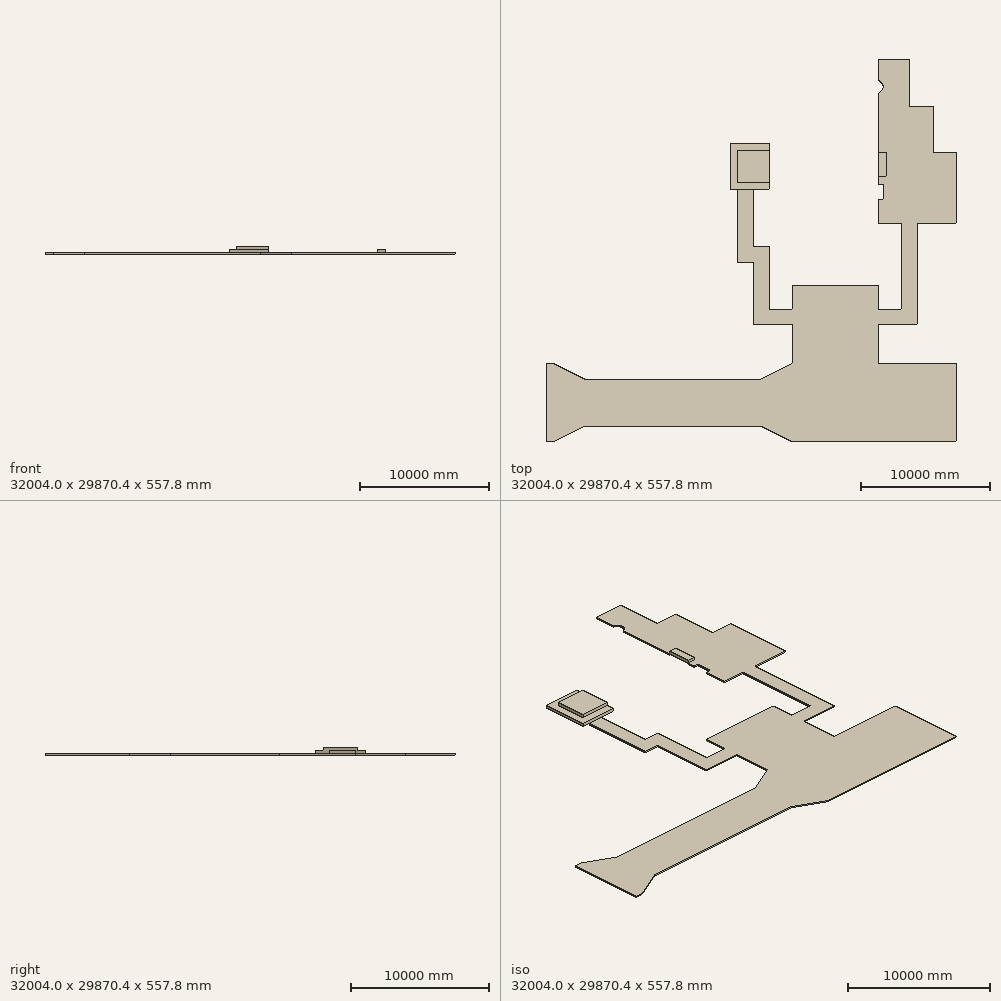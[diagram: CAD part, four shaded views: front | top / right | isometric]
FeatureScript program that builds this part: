
annotation { "Feature Type Name" : "Feature", "Feature Type Description" : "" }
export const myFeature = defineFeature(function(context is Context, id is Id, definition is map)
    precondition{}
    {
        {
            var Q0;
            Q0=qCreatedBy(makeId("Top.planeOp"),FACE);
            var sketch = newSketch(context, id + "F0", { "sketchPlane" : qUnion([Q0])});
            skLineSegment(sketch, "E0", {"start": v(0, 0) * mm, "end": v(-6705.6, 0) * mm});
            skLineSegment(sketch, "E1", {"start": v(-6705.6, 0) * mm, "end": v(-6705.6, 6705.6) * mm, "construction": true});
            skLineSegment(sketch, "E2", {"start": v(-6705.6, 6705.6) * mm, "end": v(-8534.4, 6705.6) * mm, "construction": true});
            skLineSegment(sketch, "E3", {"start": v(-8534.4, 6705.6) * mm, "end": v(-8534.4, 17678.4) * mm, "construction": true});
            skLineSegment(sketch, "E4", {"start": v(-8534.4, 17678.4) * mm, "end": v(0, 17678.4) * mm, "construction": true});
            skLineSegment(sketch, "E5", {"start": v(0, 17678.4) * mm, "end": v(0, 7924.8) * mm});
            skLineSegment(sketch, "E6", {"start": v(-9753.6, 3048) * mm, "end": v(-9753.6, 7467.6) * mm});
            skLineSegment(sketch, "E7", {"start": v(-11582.4, 7467.6) * mm, "end": v(-8534.4, 7467.6) * mm});
            skLineSegment(sketch, "E8", {"start": v(-8534.4, 7467.6) * mm, "end": v(-8534.4, 11125.2) * mm});
            skLineSegment(sketch, "E9", {"start": v(-8534.4, 11125.2) * mm, "end": v(-11582.4, 11125.2) * mm});
            skLineSegment(sketch, "E10", {"start": v(-10972.8, 7467.6) * mm, "end": v(-10972.8, 1828.8) * mm});
            skLineSegment(sketch, "E11", {"start": v(-10972.8, 1828.8) * mm, "end": v(-9753.6, 1828.8) * mm});
            skLineSegment(sketch, "E12", {"start": v(-6705.6, -3048) * mm, "end": v(-6705.6, -6096) * mm});
            skLineSegment(sketch, "E13", {"start": v(-25298.4, -6096) * mm, "end": v(-25908, -6096) * mm});
            skLineSegment(sketch, "E14", {"start": v(-25908, -6096) * mm, "end": v(-25908, -12192) * mm});
            skLineSegment(sketch, "E15", {"start": v(-25908, -12192) * mm, "end": v(-25298.4, -12192) * mm});
            skLineSegment(sketch, "E16", {"start": v(-6705.6, -12192) * mm, "end": v(6096, -12192) * mm});
            skLineSegment(sketch, "E17", {"start": v(6096, -12192) * mm, "end": v(6096, -6096) * mm});
            skLineSegment(sketch, "E18", {"start": v(6096, -6096) * mm, "end": v(0, -6096) * mm});
            skLineSegment(sketch, "E19", {"start": v(0, -6096) * mm, "end": v(0, -3048) * mm});
            skLineSegment(sketch, "E20", {"start": v(0, -3048) * mm, "end": v(3048, -3048) * mm});
            skLineSegment(sketch, "E21", {"start": v(3048, -3048) * mm, "end": v(3048, 4876.8) * mm});
            skLineSegment(sketch, "E22", {"start": v(3048, 4876.8) * mm, "end": v(4267.2, 4876.8) * mm});
            skLineSegment(sketch, "E23", {"start": v(4267.2, 4876.8) * mm, "end": v(4267.2, 4876.8) * mm});
            skLineSegment(sketch, "E24", {"start": v(4267.2, 4876.8) * mm, "end": v(6096, 4876.8) * mm});
            skLineSegment(sketch, "E25", {"start": v(2438.4, 17678.4) * mm, "end": v(0, 17678.4) * mm});
            skLineSegment(sketch, "E26.bottom", {"start": v(-8534.4, 8839.2) * mm, "end": v(-8382, 8839.2) * mm, "construction": true});
            skLineSegment(sketch, "E26.top", {"start": v(-8534.4, 9753.6) * mm, "end": v(-8382, 9753.6) * mm, "construction": true});
            skLineSegment(sketch, "E26.right", {"start": v(-8382, 8839.2) * mm, "end": v(-8382, 9753.6) * mm, "construction": true});
            skLineSegment(sketch, "E27", {"start": v(0, 14020.8) * mm, "end": v(457.2, 13106.4) * mm});
            skLineSegment(sketch, "E28", {"start": v(457.2, 13106.4) * mm, "end": v(457.2, 11277.6) * mm});
            skLineSegment(sketch, "E29", {"start": v(457.2, 11277.6) * mm, "end": v(0, 10363.2) * mm});
            skLineSegment(sketch, "E30.bottom", {"start": v(0, 6324.6) * mm, "end": v(-152.4, 6324.6) * mm, "construction": true});
            skLineSegment(sketch, "E30.top", {"start": v(0, 5410.2) * mm, "end": v(-152.4, 5410.2) * mm, "construction": true});
            skLineSegment(sketch, "E30.left", {"start": v(0, 6324.6) * mm, "end": v(0, 5410.2) * mm, "construction": true});
            skLineSegment(sketch, "E30.right", {"start": v(-152.4, 6324.6) * mm, "end": v(-152.4, 5410.2) * mm, "construction": true});
            skLineSegment(sketch, "E31.bottom", {"start": v(0, 10134.6) * mm, "end": v(-152.4, 10134.6) * mm, "construction": true});
            skLineSegment(sketch, "E31.top", {"start": v(0, 9372.6) * mm, "end": v(-152.4, 9372.6) * mm, "construction": true});
            skLineSegment(sketch, "E31.left", {"start": v(0, 10134.6) * mm, "end": v(0, 9372.6) * mm, "construction": true});
            skLineSegment(sketch, "E31.right", {"start": v(-152.4, 10134.6) * mm, "end": v(-152.4, 9372.6) * mm, "construction": true});
            skLineSegment(sketch, "E32.bottom", {"start": v(0, 10363.2) * mm, "end": v(609.6, 10363.2) * mm});
            skLineSegment(sketch, "E32.top", {"start": v(0, 8534.4) * mm, "end": v(609.6, 8534.4) * mm});
            skLineSegment(sketch, "E32.left", {"start": v(0, 10363.2) * mm, "end": v(0, 8534.4) * mm});
            skLineSegment(sketch, "E32.right", {"start": v(609.6, 10363.2) * mm, "end": v(609.6, 8534.4) * mm});
            skLineSegment(sketch, "E33", {"start": v(0, 7924.8) * mm, "end": v(381, 7924.8) * mm});
            skLineSegment(sketch, "E34", {"start": v(381, 7924.8) * mm, "end": v(381, 6705.6) * mm});
            skLineSegment(sketch, "E35", {"start": v(381, 6705.6) * mm, "end": v(0, 6705.6) * mm});
            skLineSegment(sketch, "E36.trimOffspring", {"start": v(0, 6705.6) * mm, "end": v(0, 4876.8) * mm});
            skArc(sketch, "E37", {"start": v(0, 15011.4) * mm, "mid": v(381, 15506.7) * mm, "end": v(0, 16002) * mm});
            skLineSegment(sketch, "E38", {"start": v(-9144, -10972.8) * mm, "end": v(-22860, -10972.8) * mm});
            skLineSegment(sketch, "E39", {"start": v(6096, 10363.2) * mm, "end": v(6096, 4876.8) * mm});
            skLineSegment(sketch, "E40.bottom", {"start": v(3780.64, 8654.36) * mm, "end": v(4695.04, 8654.36) * mm, "construction": true});
            skLineSegment(sketch, "E40.top", {"start": v(3780.64, 6825.56) * mm, "end": v(4695.04, 6825.56) * mm, "construction": true});
            skLineSegment(sketch, "E40.left", {"start": v(3780.64, 8654.36) * mm, "end": v(3780.64, 6825.56) * mm, "construction": true});
            skLineSegment(sketch, "E40.right", {"start": v(4695.04, 8654.36) * mm, "end": v(4695.04, 6825.56) * mm, "construction": true});
            skLineSegment(sketch, "E41.bottom", {"start": v(4787.31, 6825.56) * mm, "end": v(5396.91, 6825.56) * mm, "construction": true});
            skLineSegment(sketch, "E41.top", {"start": v(4787.31, 7435.16) * mm, "end": v(5396.91, 7435.16) * mm, "construction": true});
            skLineSegment(sketch, "E41.left", {"start": v(4787.31, 6825.56) * mm, "end": v(4787.31, 7435.16) * mm, "construction": true});
            skLineSegment(sketch, "E41.right", {"start": v(5396.91, 6825.56) * mm, "end": v(5396.91, 7435.16) * mm, "construction": true});
            skLineSegment(sketch, "E42.bottom", {"start": v(4864.53, 8404.24) * mm, "end": v(5474.13, 8404.24) * mm, "construction": true});
            skLineSegment(sketch, "E42.top", {"start": v(4864.53, 7794.64) * mm, "end": v(5474.13, 7794.64) * mm, "construction": true});
            skLineSegment(sketch, "E42.left", {"start": v(4864.53, 8404.24) * mm, "end": v(4864.53, 7794.64) * mm, "construction": true});
            skLineSegment(sketch, "E42.right", {"start": v(5474.13, 8404.24) * mm, "end": v(5474.13, 7794.64) * mm, "construction": true});
            skLineSegment(sketch, "E43.bottom", {"start": v(2996.04, 8455.63) * mm, "end": v(3605.64, 8455.63) * mm, "construction": true});
            skLineSegment(sketch, "E43.top", {"start": v(2996.04, 7846.03) * mm, "end": v(3605.64, 7846.03) * mm, "construction": true});
            skLineSegment(sketch, "E43.left", {"start": v(2996.04, 8455.63) * mm, "end": v(2996.04, 7846.03) * mm, "construction": true});
            skLineSegment(sketch, "E43.right", {"start": v(3605.64, 8455.63) * mm, "end": v(3605.64, 7846.03) * mm, "construction": true});
            skLineSegment(sketch, "E44.bottom", {"start": v(3054.53, 7634.15) * mm, "end": v(3664.13, 7634.15) * mm, "construction": true});
            skLineSegment(sketch, "E44.top", {"start": v(3054.53, 7024.55) * mm, "end": v(3664.13, 7024.55) * mm, "construction": true});
            skLineSegment(sketch, "E44.left", {"start": v(3054.53, 7634.15) * mm, "end": v(3054.53, 7024.55) * mm, "construction": true});
            skLineSegment(sketch, "E44.right", {"start": v(3664.13, 7634.15) * mm, "end": v(3664.13, 7024.55) * mm, "construction": true});
            skLineSegment(sketch, "E45.bottom", {"start": v(4003.05, 6673.38) * mm, "end": v(4612.65, 6673.38) * mm, "construction": true});
            skLineSegment(sketch, "E45.top", {"start": v(4003.05, 6063.78) * mm, "end": v(4612.65, 6063.78) * mm, "construction": true});
            skLineSegment(sketch, "E45.left", {"start": v(4003.05, 6673.38) * mm, "end": v(4003.05, 6063.78) * mm, "construction": true});
            skLineSegment(sketch, "E45.right", {"start": v(4612.65, 6673.38) * mm, "end": v(4612.65, 6063.78) * mm, "construction": true});
            skLineSegment(sketch, "E46.bottom", {"start": v(3897.7, 9487.56) * mm, "end": v(4507.3, 9487.56) * mm, "construction": true});
            skLineSegment(sketch, "E46.top", {"start": v(3897.7, 8877.96) * mm, "end": v(4507.3, 8877.96) * mm, "construction": true});
            skLineSegment(sketch, "E46.left", {"start": v(3897.7, 9487.56) * mm, "end": v(3897.7, 8877.96) * mm, "construction": true});
            skLineSegment(sketch, "E46.right", {"start": v(4507.3, 9487.56) * mm, "end": v(4507.3, 8877.96) * mm, "construction": true});
            skLineSegment(sketch, "E47.bottom", {"start": v(538.11, 7676.63) * mm, "end": v(1071.51, 7676.63) * mm, "construction": true});
            skLineSegment(sketch, "E47.top", {"start": v(538.11, 6762.23) * mm, "end": v(1071.51, 6762.23) * mm, "construction": true});
            skLineSegment(sketch, "E47.left", {"start": v(538.11, 7676.63) * mm, "end": v(538.11, 6762.23) * mm, "construction": true});
            skLineSegment(sketch, "E47.right", {"start": v(1071.51, 7676.63) * mm, "end": v(1071.51, 6762.23) * mm, "construction": true});
            skLineSegment(sketch, "E48", {"start": v(4267.2, 14020.8) * mm, "end": v(4267.2, 10363.2) * mm});
            skLineSegment(sketch, "E49", {"start": v(4267.2, 10363.2) * mm, "end": v(6096, 10363.2) * mm});
            skCircle(sketch, "E50", {"center": v(2438.4, 12183.95) * mm, "radius": 609.6 * mm, "construction": true});
            skLineSegment(sketch, "E51.bottom", {"start": v(2960.5, 11445.2) * mm, "end": v(3570.1, 11445.2) * mm, "construction": true});
            skLineSegment(sketch, "E51.top", {"start": v(2960.5, 10835.6) * mm, "end": v(3570.1, 10835.6) * mm, "construction": true});
            skLineSegment(sketch, "E51.left", {"start": v(2960.5, 11445.2) * mm, "end": v(2960.5, 10835.6) * mm, "construction": true});
            skLineSegment(sketch, "E51.right", {"start": v(3570.1, 11445.2) * mm, "end": v(3570.1, 10835.6) * mm, "construction": true});
            skLineSegment(sketch, "E52.bottom", {"start": v(2962.13, 13403.32) * mm, "end": v(3571.73, 13403.32) * mm, "construction": true});
            skLineSegment(sketch, "E52.top", {"start": v(2962.13, 12793.72) * mm, "end": v(3571.73, 12793.72) * mm, "construction": true});
            skLineSegment(sketch, "E52.left", {"start": v(2962.13, 13403.32) * mm, "end": v(2962.13, 12793.72) * mm, "construction": true});
            skLineSegment(sketch, "E52.right", {"start": v(3571.73, 13403.32) * mm, "end": v(3571.73, 12793.72) * mm, "construction": true});
            skLineSegment(sketch, "E53.bottom", {"start": v(1269.31, 13348.42) * mm, "end": v(1878.91, 13348.42) * mm, "construction": true});
            skLineSegment(sketch, "E53.top", {"start": v(1269.31, 12738.82) * mm, "end": v(1878.91, 12738.82) * mm, "construction": true});
            skLineSegment(sketch, "E53.left", {"start": v(1269.31, 13348.42) * mm, "end": v(1269.31, 12738.82) * mm, "construction": true});
            skLineSegment(sketch, "E53.right", {"start": v(1878.91, 13348.42) * mm, "end": v(1878.91, 12738.82) * mm, "construction": true});
            skLineSegment(sketch, "E54.bottom", {"start": v(1281.83, 11466.17) * mm, "end": v(1891.43, 11466.17) * mm, "construction": true});
            skLineSegment(sketch, "E54.top", {"start": v(1281.83, 10856.57) * mm, "end": v(1891.43, 10856.57) * mm, "construction": true});
            skLineSegment(sketch, "E54.left", {"start": v(1281.83, 11466.17) * mm, "end": v(1281.83, 10856.57) * mm, "construction": true});
            skLineSegment(sketch, "E54.right", {"start": v(1891.43, 11466.17) * mm, "end": v(1891.43, 10856.57) * mm, "construction": true});
            skLineSegment(sketch, "E55", {"start": v(2438.4, 17678.4) * mm, "end": v(2438.4, 14020.8) * mm});
            skLineSegment(sketch, "E56", {"start": v(2438.4, 14020.8) * mm, "end": v(4267.2, 14020.8) * mm});
            skLineSegment(sketch, "E57", {"start": v(-11582.4, 11125.2) * mm, "end": v(-11582.4, 7467.6) * mm});
            skLineSegment(sketch, "E58", {"start": v(-8534.4, 3048) * mm, "end": v(-8534.4, -1828.8) * mm});
            skLineSegment(sketch, "E59", {"start": v(-8534.4, -1828.8) * mm, "end": v(-6705.6, -1828.8) * mm});
            skLineSegment(sketch, "E60", {"start": v(-6705.6, -1828.8) * mm, "end": v(-6705.6, 0) * mm});
            skLineSegment(sketch, "E61", {"start": v(-9753.6, 1828.8) * mm, "end": v(-9753.6, -3048) * mm});
            skLineSegment(sketch, "E62", {"start": v(-9753.6, -3048) * mm, "end": v(-6705.6, -3048) * mm});
            skLineSegment(sketch, "E63", {"start": v(0, 4876.8) * mm, "end": v(1828.8, 4876.8) * mm});
            skLineSegment(sketch, "E64", {"start": v(1828.8, 4876.8) * mm, "end": v(1828.8, -1828.8) * mm});
            skLineSegment(sketch, "E65", {"start": v(1828.8, -1828.8) * mm, "end": v(0, -1828.8) * mm});
            skLineSegment(sketch, "E66", {"start": v(0, -1828.8) * mm, "end": v(0, 0) * mm});
            skLineSegment(sketch, "E67", {"start": v(-8534.4, 3048) * mm, "end": v(-9753.6, 3048) * mm});
            skLineSegment(sketch, "E68", {"start": v(0, 0) * mm, "end": v(0, 4876.8) * mm, "construction": true});
            skLineSegment(sketch, "E69", {"start": v(-8534.4, 10515.6) * mm, "end": v(-10972.8, 10515.6) * mm});
            skLineSegment(sketch, "E70", {"start": v(-10972.8, 10515.6) * mm, "end": v(-10972.8, 8077.2) * mm});
            skLineSegment(sketch, "E71", {"start": v(-10972.8, 8077.2) * mm, "end": v(-8534.4, 8077.2) * mm});
            skLineSegment(sketch, "E72", {"start": v(-25298.4, -6096) * mm, "end": v(-22860, -7315.2) * mm});
            skLineSegment(sketch, "E73", {"start": v(-25298.4, -12192) * mm, "end": v(-22860, -10972.8) * mm});
            skLineSegment(sketch, "E74", {"start": v(-6705.6, -6096) * mm, "end": v(-9144, -7315.2) * mm});
            skLineSegment(sketch, "E75", {"start": v(-6705.6, -12192) * mm, "end": v(-9144, -10972.8) * mm});
            skLineSegment(sketch, "E76", {"start": v(-22860, -7315.2) * mm, "end": v(-9144, -7315.2) * mm});
            skCircle(sketch, "E77", {"center": v(1219.2, 15837.4) * mm, "radius": 826 * mm, "construction": true});
            skLineSegment(sketch, "E78", {"start": v(879.35, 15084.55) * mm, "end": v(879.35, 14020.8) * mm, "construction": true});
            skLineSegment(sketch, "E79", {"start": v(879.35, 14020.8) * mm, "end": v(1559.05, 14020.8) * mm, "construction": true});
            skLineSegment(sketch, "E80", {"start": v(1559.05, 14020.8) * mm, "end": v(1559.05, 15084.55) * mm, "construction": true});
            skLineSegment(sketch, "E81", {"start": v(691.9, 16473.2) * mm, "end": v(691.9, 17513.8) * mm, "construction": true});
            skLineSegment(sketch, "E82", {"start": v(691.9, 17513.8) * mm, "end": v(1746.5, 17513.8) * mm, "construction": true});
            skLineSegment(sketch, "E83", {"start": v(1746.5, 17513.8) * mm, "end": v(1746.5, 16473.2) * mm, "construction": true});
            skSolve(sketch);
        }
        {
            var Q0;
            Q0=makeQuery(id+"F0.imprint","IMPRINT",FACE,{"disambiguationData":[TD([[makeQuery(id+"F0.imprint","IMPRINT",EDGE,{"derivedFrom":sQuery(id+"F0.wireOp",EDGE,"E0")}),1.0]])]});
            var Q1;
            {var subQ0=sQuery(id+"F0.wireOp",EDGE,"E27");Q1=makeQuery(id+"F0.imprint","IMPRINT",FACE,{"disambiguationData":[TD([[makeQuery(id+"F0.imprint","IMPRINT",EDGE,{"derivedFrom":subQ0}),-1.0]])]});}
            extrude(context, id + "F1", {"entities" : qUnion([Q0, Q1]), "oppositeDirection" : true, "depth" : 100.58 * mm});
        }
        {
            var Q0;
            Q0=makeQuery(id+"F0.imprint","IMPRINT",FACE,{"disambiguationData":[TD([[makeQuery(id+"F0.imprint","IMPRINT",EDGE,{"derivedFrom":sQuery(id+"F0.wireOp",EDGE,"VFPwrc4Q-GK3d-vJYQ-qDZh-QmO6r3FZWh0v.bottom")}),1.0]])]});
            var Q1;
            Q1=makeQuery(id+"F0.imprint","IMPRINT",FACE,{"disambiguationData":[TD([[makeQuery(id+"F0.imprint","IMPRINT",EDGE,{"derivedFrom":sQuery(id+"F0.wireOp",EDGE,"E32.bottom")}),-1.0]])]});
            var Q2;
            {var subQ1=sQuery(id+"F0.wireOp",EDGE,"E8");Q2=makeQuery(id+"F0.imprint","IMPRINT",FACE,{"disambiguationData":[TD([[makeQuery(id+"F0.imprint","IMPRINT",EDGE,{"derivedFrom":subQ1}),1.0]])]});}
            extrude(context, id + "F2", {"entities" : qUnion([Q0, Q1, Q2]), "operationType" : NewBodyOperationType.ADD, "depth" : 228.6 * mm});
        }
        {
            var Q0;
            {var subQ0=sQuery(id+"F0.wireOp",EDGE,"E69");Q0=makeQuery(id+"F0.imprint","IMPRINT",FACE,{"disambiguationData":[TD([[makeQuery(id+"F0.imprint","IMPRINT",EDGE,{"derivedFrom":subQ0}),1.0]])]});}
            extrude(context, id + "F3", {"entities" : qUnion([Q0]), "operationType" : NewBodyOperationType.ADD, "depth" : 457.2 * mm});
        }
    });
